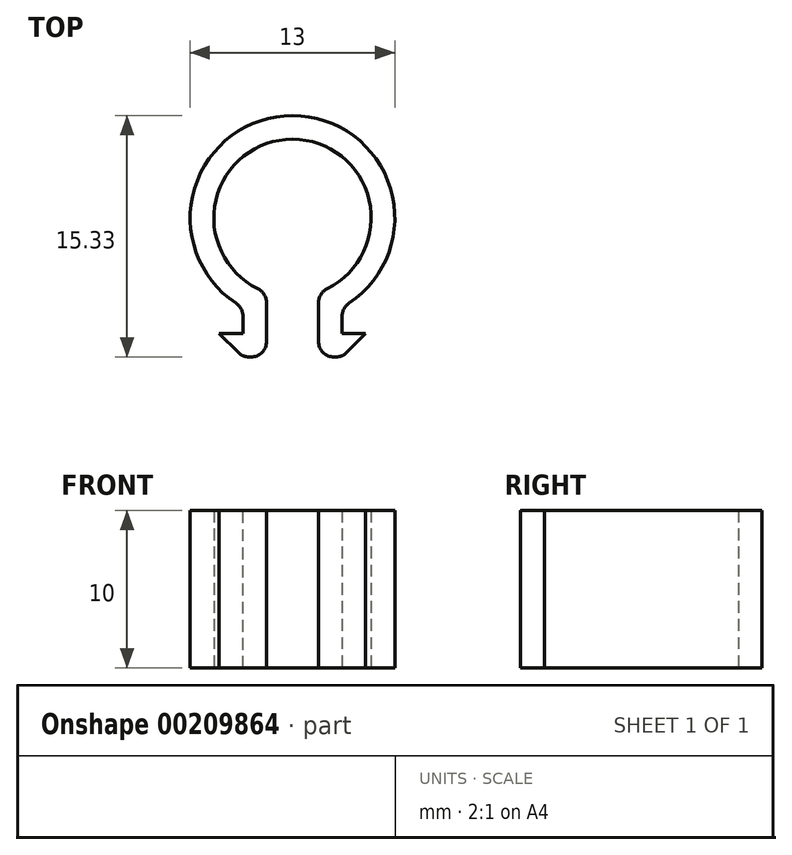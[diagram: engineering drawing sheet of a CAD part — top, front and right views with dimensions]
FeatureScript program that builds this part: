
annotation { "Feature Type Name" : "Feature", "Feature Type Description" : "" }
export const myFeature = defineFeature(function(context is Context, id is Id, definition is map)
    precondition{}
    {
        {
            var Q0;
            Q0=qCreatedBy(makeId("Top.planeOp"),FACE);
            var sketch = newSketch(context, id + "F0", { "sketchPlane" : qUnion([Q0])});
            skCircle(sketch, "E0", {"center": v(-40.2, 28.77) * mm, "radius": 5 * mm});
            skCircle(sketch, "E1", {"center": v(-40.2, 28.77) * mm, "radius": 6.5 * mm});
            skLineSegment(sketch, "E2", {"start": v(-41.86, 24.05) * mm, "end": v(-41.86, 19.94) * mm});
            skLineSegment(sketch, "E3", {"start": v(-40.2, 28.77) * mm, "end": v(-40.2, 11.73) * mm, "construction": true});
            skLineSegment(sketch, "E4", {"start": v(-43.36, 23.09) * mm, "end": v(-43.36, 19.94) * mm});
            skLineSegment(sketch, "E5", {"start": v(-43.36, 19.94) * mm, "end": v(-41.86, 19.94) * mm});
            skLineSegment(sketch, "E6", {"start": v(-43.36, 21.44) * mm, "end": v(-44.86, 21.44) * mm});
            skLineSegment(sketch, "E7", {"start": v(-44.86, 21.44) * mm, "end": v(-43.36, 19.94) * mm});
            skLineSegment(sketch, "E8", {"start": v(-38.56, 24.05) * mm, "end": v(-38.56, 19.94) * mm});
            skLineSegment(sketch, "E9", {"start": v(-38.56, 19.94) * mm, "end": v(-37.06, 19.94) * mm});
            skLineSegment(sketch, "E10", {"start": v(-37.06, 19.94) * mm, "end": v(-35.56, 21.44) * mm});
            skLineSegment(sketch, "E11", {"start": v(-37.06, 23.09) * mm, "end": v(-37.06, 19.94) * mm});
            skLineSegment(sketch, "E12", {"start": v(-35.56, 21.44) * mm, "end": v(-37.06, 21.44) * mm});
            skPoint(sketch, "E13", {"position": v(-41.86, 22.48) * mm});
            skPoint(sketch, "E14", {"position": v(-38.56, 22.48) * mm});
            skSolve(sketch);
        }
        {
            var Q0;
            {var subQ5=sQuery(id+"F0.wireOp",EDGE,"E2");var subQ7=sQuery(id+"F0.wireOp",EDGE,"E0");var subQ8=makeQuery(id+"F0.imprint","INTERSECT",VERTEX,{"derivedFrom":[subQ7,subQ5]});Q0=makeQuery(id+"F0.imprint","IMPRINT",FACE,{"disambiguationData":[TD([[makeQuery(id+"F0.imprint","IMPRINT",EDGE,{"disambiguationData":[TD([[subQ8,1.0]])],"derivedFrom":subQ7}),-1.0]])]});}
            var Q1;
            {var subQ4=sQuery(id+"F0.wireOp",EDGE,"E9");Q1=makeQuery(id+"F0.imprint","IMPRINT",FACE,{"disambiguationData":[TD([[makeQuery(id+"F0.imprint","IMPRINT",EDGE,{"derivedFrom":subQ4}),1.0]])]});}
            var Q2;
            {var subQ0=sQuery(id+"F0.wireOp",EDGE,"E5");Q2=makeQuery(id+"F0.imprint","IMPRINT",FACE,{"disambiguationData":[TD([[makeQuery(id+"F0.imprint","IMPRINT",EDGE,{"derivedFrom":subQ0}),1.0]])]});}
            var Q3;
            {var subQ2=sQuery(id+"F0.wireOp",EDGE,"E6");Q3=makeQuery(id+"F0.imprint","IMPRINT",FACE,{"disambiguationData":[TD([[makeQuery(id+"F0.imprint","IMPRINT",EDGE,{"derivedFrom":subQ2}),1.0]])]});}
            var Q4;
            {var subQ0=sQuery(id+"F0.wireOp",EDGE,"E10");Q4=makeQuery(id+"F0.imprint","IMPRINT",FACE,{"disambiguationData":[TD([[makeQuery(id+"F0.imprint","IMPRINT",EDGE,{"derivedFrom":subQ0}),1.0]])]});}
            extrude(context, id + "F1", {"entities" : qUnion([Q0, Q1, Q2, Q3, Q4]), "depth" : 10 * mm});
        }
        {
            var Q0;
            Q0=makeQuery(id+"F1.opExtrude","SWEPT_EDGE",EDGE,{"disambiguationData":[OSD([sQuery(id+"F0.wireOp",EDGE,"E4"),sQuery(id+"F0.wireOp",EDGE,"E5"),sQuery(id+"F0.wireOp",EDGE,"E7")])]});
            var Q1;
            Q1=makeQuery(id+"F1.opExtrude","SWEPT_EDGE",EDGE,{"disambiguationData":[OSD([sQuery(id+"F0.wireOp",EDGE,"E9"),sQuery(id+"F0.wireOp",EDGE,"E10"),sQuery(id+"F0.wireOp",EDGE,"E11")])]});
            var Q2;
            Q2=makeQuery(id+"F1.opExtrude","SWEPT_EDGE",EDGE,{"disambiguationData":[OSD([sQuery(id+"F0.wireOp",EDGE,"E2"),sQuery(id+"F0.wireOp",EDGE,"E5")])]});
            var Q3;
            Q3=makeQuery(id+"F1.opExtrude","SWEPT_EDGE",EDGE,{"disambiguationData":[OSD([sQuery(id+"F0.wireOp",EDGE,"E0"),sQuery(id+"F0.wireOp",EDGE,"E2")])]});
            var Q4;
            Q4=makeQuery(id+"F1.opExtrude","SWEPT_EDGE",EDGE,{"disambiguationData":[OSD([sQuery(id+"F0.wireOp",EDGE,"E1"),sQuery(id+"F0.wireOp",EDGE,"E11")])]});
            var Q5;
            Q5=makeQuery(id+"F1.opExtrude","SWEPT_EDGE",EDGE,{"disambiguationData":[OSD([sQuery(id+"F0.wireOp",EDGE,"E1"),sQuery(id+"F0.wireOp",EDGE,"E4")])]});
            var Q6;
            Q6=makeQuery(id+"F1.opExtrude","SWEPT_EDGE",EDGE,{"disambiguationData":[OSD([sQuery(id+"F0.wireOp",EDGE,"E0"),sQuery(id+"F0.wireOp",EDGE,"E8")])]});
            var Q7;
            Q7=makeQuery(id+"F1.opExtrude","SWEPT_EDGE",EDGE,{"disambiguationData":[OSD([sQuery(id+"F0.wireOp",EDGE,"E8"),sQuery(id+"F0.wireOp",EDGE,"E9")])]});
            fillet(context, id + "F2", {"entities" : qUnion([Q0, Q1, Q2, Q3, Q4, Q5, Q6, Q7]), "radius" : 1 * mm, "tangentPropagation" : true, "allowEdgeOverflow" : false});
        }
    });
